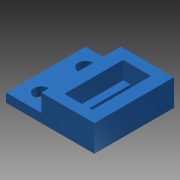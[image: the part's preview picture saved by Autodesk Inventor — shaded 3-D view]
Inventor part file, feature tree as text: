
AUTODESK INVENTOR PART (.ipt)
format: ipt  version: 2013 (Build 170138000, 138)  size: 102,912 bytes
history: native  units: mm
features: extrude x2, sketch x1
ambient origin geometry x8: Origin, YZ Plane, XZ Plane, XY Plane, X Axis, Y Axis, Z Axis, Center Point
bodies: Solid1 (feature_tree)
feature tree (3):
  sketch  "Sketch1"  dims[d0=20.0mm d1=18.0mm d3=3.0mm d5=3.4mm d6=3.4mm d7=4.0mm d8=4.0mm d9=10.0mm d10=2.0mm d11=0.0mm d20=12.0mm d21=6.3mm d22=13.3mm d23=6.0mm d24=0.0mm]
  extrude  "Extrusion1"  Depth=18.0mm
  extrude  "Extrusion3"  Depth=3.0mm
